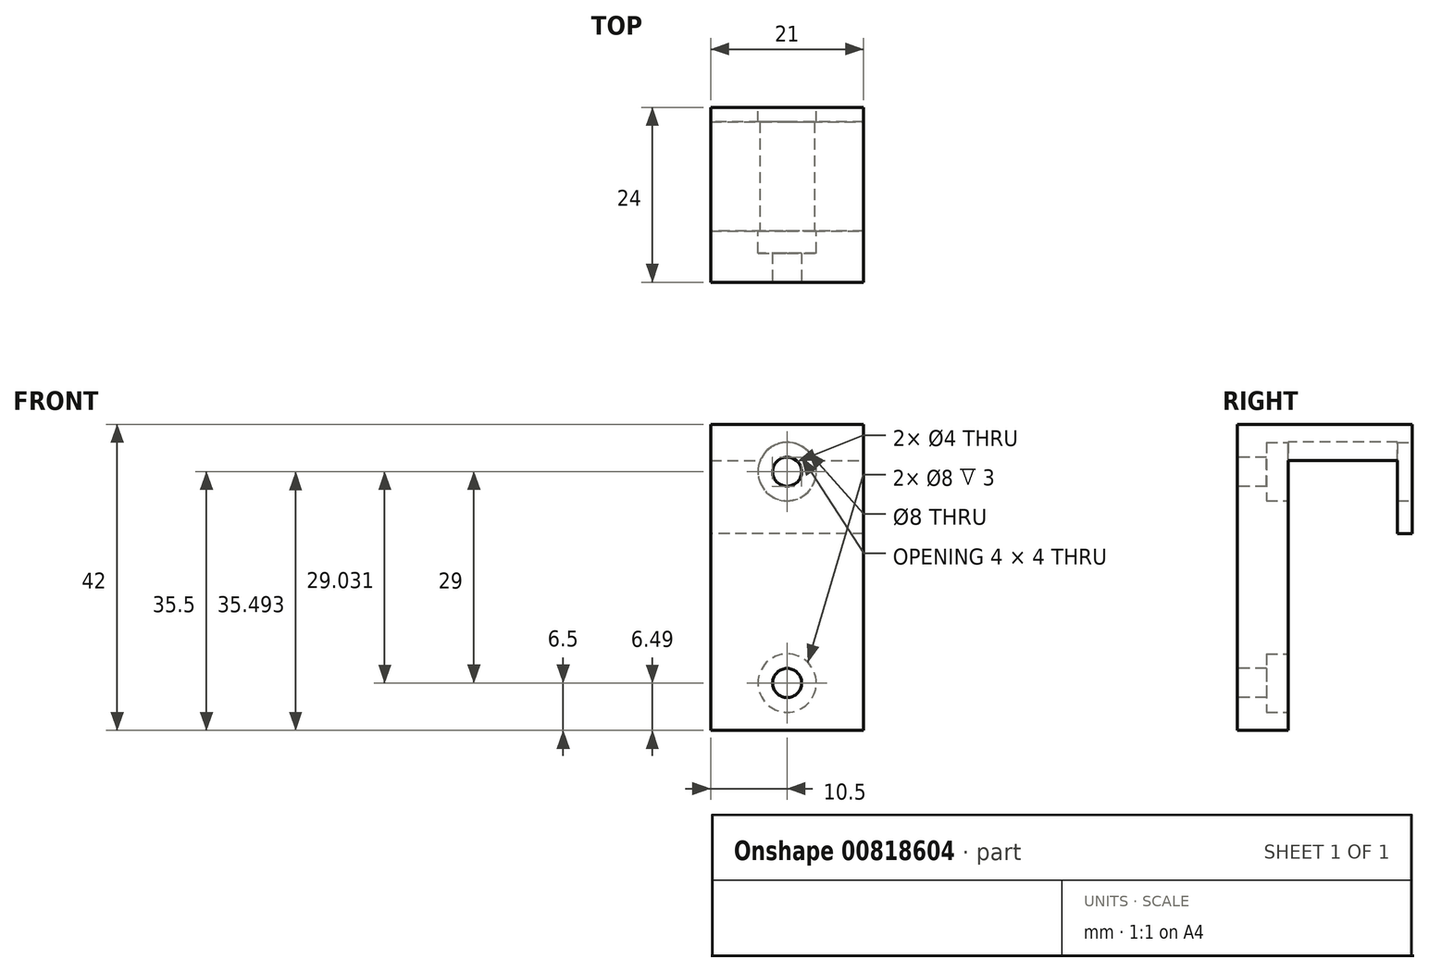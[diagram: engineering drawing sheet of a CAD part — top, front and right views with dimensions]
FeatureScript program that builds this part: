
annotation { "Feature Type Name" : "Feature", "Feature Type Description" : "" }
export const myFeature = defineFeature(function(context is Context, id is Id, definition is map)
    precondition{}
    {
        {
            var Q0;
            Q0=qCreatedBy(makeId("Front.planeOp"),FACE);
            var sketch = newSketch(context, id + "F0", { "sketchPlane" : qUnion([Q0])});
            skLineSegment(sketch, "E0.bottom", {"start": v(10.5, -21) * mm, "end": v(-10.5, -21) * mm});
            skLineSegment(sketch, "E0.top", {"start": v(10.5, 21) * mm, "end": v(-10.5, 21) * mm});
            skLineSegment(sketch, "E0.left", {"start": v(10.5, -21) * mm, "end": v(10.5, 21) * mm});
            skLineSegment(sketch, "E0.right", {"start": v(-10.5, -21) * mm, "end": v(-10.5, 21) * mm});
            skPoint(sketch, "E0.middle", {"position": v(0, 0) * mm});
            skSolve(sketch);
        }
        {
            var Q0;
            Q0=makeQuery(id+"F0.imprint","IMPRINT",FACE,{"disambiguationData":[TD([[makeQuery(id+"F0.imprint","IMPRINT",EDGE,{"derivedFrom":sQuery(id+"F0.wireOp",EDGE,"E0.bottom")}),-1.0]])]});
            extrude(context, id + "F1", {"entities" : qUnion([Q0]), "depth" : 7 * mm, "offsetDistance" : 25 * mm});
        }
        {
            var Q0;
            Q0=makeQuery(id+"F1.opExtrude","CAP_FACE",FACE,{"disambiguationData":[OSD([sQuery(id+"F0.wireOp",EDGE,"E0.bottom"),sQuery(id+"F0.wireOp",EDGE,"E0.top"),sQuery(id+"F0.wireOp",EDGE,"E0.left"),sQuery(id+"F0.wireOp",EDGE,"E0.right")])],"isStart":true});
            var sketch = newSketch(context, id + "F2", { "sketchPlane" : qUnion([Q0])});
            skLineSegment(sketch, "E1.bottom", {"start": v(10.5, 21) * mm, "end": v(-10.5, 21) * mm});
            skLineSegment(sketch, "E1.top", {"start": v(10.5, 16) * mm, "end": v(-10.5, 16) * mm});
            skLineSegment(sketch, "E1.left", {"start": v(10.5, 21) * mm, "end": v(10.5, 16) * mm});
            skLineSegment(sketch, "E1.right", {"start": v(-10.5, 21) * mm, "end": v(-10.5, 16) * mm});
            skSolve(sketch);
        }
        {
            var Q0;
            Q0=makeQuery(id+"F2.imprint","IMPRINT",FACE,{"disambiguationData":[TD([[makeQuery(id+"F2.imprint","IMPRINT",EDGE,{"derivedFrom":sQuery(id+"F2.wireOp",EDGE,"E1.bottom")}),-1.0]])]});
            extrude(context, id + "F3", {"entities" : qUnion([Q0]), "operationType" : NewBodyOperationType.ADD, "depth" : 17 * mm, "offsetDistance" : 25 * mm});
        }
        {
            var Q0;
            Q0=makeQuery(id+"F1.opExtrude","CAP_FACE",FACE,{"disambiguationData":[OSD([sQuery(id+"F0.wireOp",EDGE,"E0.bottom"),sQuery(id+"F0.wireOp",EDGE,"E0.top"),sQuery(id+"F0.wireOp",EDGE,"E0.left"),sQuery(id+"F0.wireOp",EDGE,"E0.right")])],"isStart":false});
            var sketch = newSketch(context, id + "F4", { "sketchPlane" : qUnion([Q0])});
            skLineSegment(sketch, "E2", {"start": v(0, 21) * mm, "end": v(0, -21) * mm, "construction": true});
            skLineSegment(sketch, "E3", {"start": v(0, 21) * mm, "end": v(0, 14.5) * mm, "construction": true});
            skLineSegment(sketch, "E4", {"start": v(0, 14.5) * mm, "end": v(0, -14.5) * mm, "construction": true});
            skCircle(sketch, "E5", {"center": v(0, 14.5) * mm, "radius": 2 * mm});
            skCircle(sketch, "E6", {"center": v(0, -14.5) * mm, "radius": 2 * mm});
            skSolve(sketch);
        }
        {
            var Q0;
            Q0 = qSketchRegion(id + "F4", true);
            extrude(context, id + "F5", {"entities" : qUnion([Q0]), "operationType" : NewBodyOperationType.REMOVE, "oppositeDirection" : true, "depth" : 25 * mm, "offsetDistance" : 25 * mm});
        }
        {
            var Q0;
            {var subQ0=sQuery(id+"F2.wireOp",EDGE,"E1.top");Q0=makeQuery(id+"F2.imprint","IMPRINT",FACE,{"disambiguationData":[TD([[makeQuery(id+"F2.imprint","IMPRINT",EDGE,{"derivedFrom":subQ0}),1.0]])]});}
            var sketch = newSketch(context, id + "F6", { "sketchPlane" : qUnion([Q0])});
            skCircle(sketch, "E7", {"center": v(0, 14.52) * mm, "radius": 4 * mm});
            skCircle(sketch, "E8", {"center": v(0, -14.51) * mm, "radius": 4 * mm});
            skSolve(sketch);
        }
        {
            var Q0;
            Q0 = qSketchRegion(id + "F6", true);
            extrude(context, id + "F7", {"entities" : qUnion([Q0]), "operationType" : NewBodyOperationType.REMOVE, "oppositeDirection" : true, "depth" : 3 * mm, "offsetDistance" : 25 * mm});
        }
        {
            var Q0;
            Q0=makeQuery(id+"F0.imprint","IMPRINT",FACE,{"disambiguationData":[TD([[makeQuery(id+"F0.imprint","IMPRINT",EDGE,{"derivedFrom":sQuery(id+"F0.wireOp",EDGE,"E0.bottom")}),-1.0]])]});
            var sketch = newSketch(context, id + "F8", { "sketchPlane" : qUnion([Q0])});
            skCircle(sketch, "E9", {"center": v(0, 14.55) * mm, "radius": 4 * mm});
            skSolve(sketch);
        }
        {
            var Q0;
            Q0 = qSketchRegion(id + "F8", true);
            extrude(context, id + "F9", {"entities" : qUnion([Q0]), "operationType" : NewBodyOperationType.REMOVE, "oppositeDirection" : true, "depth" : 25 * mm, "offsetDistance" : 25 * mm});
        }
        {
            var Q0;
            Q0=makeQuery(id+"F3.boolean.opBoolean","MERGE",FACE,{"derivedFrom":[makeQuery(id+"F1.opExtrude","SWEPT_FACE",FACE,{"disambiguationData":[OSD([sQuery(id+"F0.wireOp",EDGE,"E0.top")])]}),makeQuery(id+"F3.opExtrude","SWEPT_FACE",FACE,{"disambiguationData":[OSD([sQuery(id+"F2.wireOp",EDGE,"E1.bottom")])]})]});
            var sketch = newSketch(context, id + "F10", { "sketchPlane" : qUnion([Q0])});
            skLineSegment(sketch, "E10.bottom", {"start": v(-10.5, 17) * mm, "end": v(10.5, 17) * mm});
            skLineSegment(sketch, "E10.top", {"start": v(-10.5, 15) * mm, "end": v(10.5, 15) * mm});
            skLineSegment(sketch, "E10.left", {"start": v(-10.5, 17) * mm, "end": v(-10.5, 15) * mm});
            skLineSegment(sketch, "E10.right", {"start": v(10.5, 17) * mm, "end": v(10.5, 15) * mm});
            skSolve(sketch);
        }
        {
            var Q0;
            Q0 = qSketchRegion(id + "F10", true);
            extrude(context, id + "F11", {"entities" : qUnion([Q0]), "operationType" : NewBodyOperationType.ADD, "oppositeDirection" : true, "depth" : 15 * mm, "offsetDistance" : 25 * mm});
        }
        {
            var Q0;
            Q0=makeQuery(id+"F4.imprint","IMPRINT",FACE,{"disambiguationData":[TD([[makeQuery(id+"F4.imprint","IMPRINT",EDGE,{"derivedFrom":sQuery(id+"F4.wireOp",EDGE,"E5")}),-1.0]])]});
            var sketch = newSketch(context, id + "F12", { "sketchPlane" : qUnion([Q0])});
            skCircle(sketch, "E11", {"center": v(0, 14.5) * mm, "radius": 2 * mm});
            skSolve(sketch);
        }
        {
            var Q0;
            Q0 = qSketchRegion(id + "F12", true);
            extrude(context, id + "F13", {"entities" : qUnion([Q0]), "operationType" : NewBodyOperationType.REMOVE, "oppositeDirection" : true, "depth" : 25 * mm, "offsetDistance" : 25 * mm});
        }
        {
            var Q0;
            Q0=makeQuery(id+"F11.boolean.opBoolean","MERGE",FACE,{"derivedFrom":[makeQuery(id+"F3.opExtrude","CAP_FACE",FACE,{"disambiguationData":[OSD([sQuery(id+"F2.wireOp",EDGE,"E1.bottom"),sQuery(id+"F2.wireOp",EDGE,"E1.top"),sQuery(id+"F2.wireOp",EDGE,"E1.left"),sQuery(id+"F2.wireOp",EDGE,"E1.right")])],"isStart":false}),makeQuery(id+"F11.opExtrude","SWEPT_FACE",FACE,{"disambiguationData":[OSD([sQuery(id+"F10.wireOp",EDGE,"E10.bottom")])]})]});
            var sketch = newSketch(context, id + "F14", { "sketchPlane" : qUnion([Q0])});
            skCircle(sketch, "E12", {"center": v(0, 14.5) * mm, "radius": 4 * mm});
            skSolve(sketch);
        }
        {
            var Q0;
            Q0 = qSketchRegion(id + "F14", true);
            extrude(context, id + "F15", {"entities" : qUnion([Q0]), "operationType" : NewBodyOperationType.REMOVE, "oppositeDirection" : true, "depth" : 5 * mm, "offsetDistance" : 25 * mm});
        }
    });
